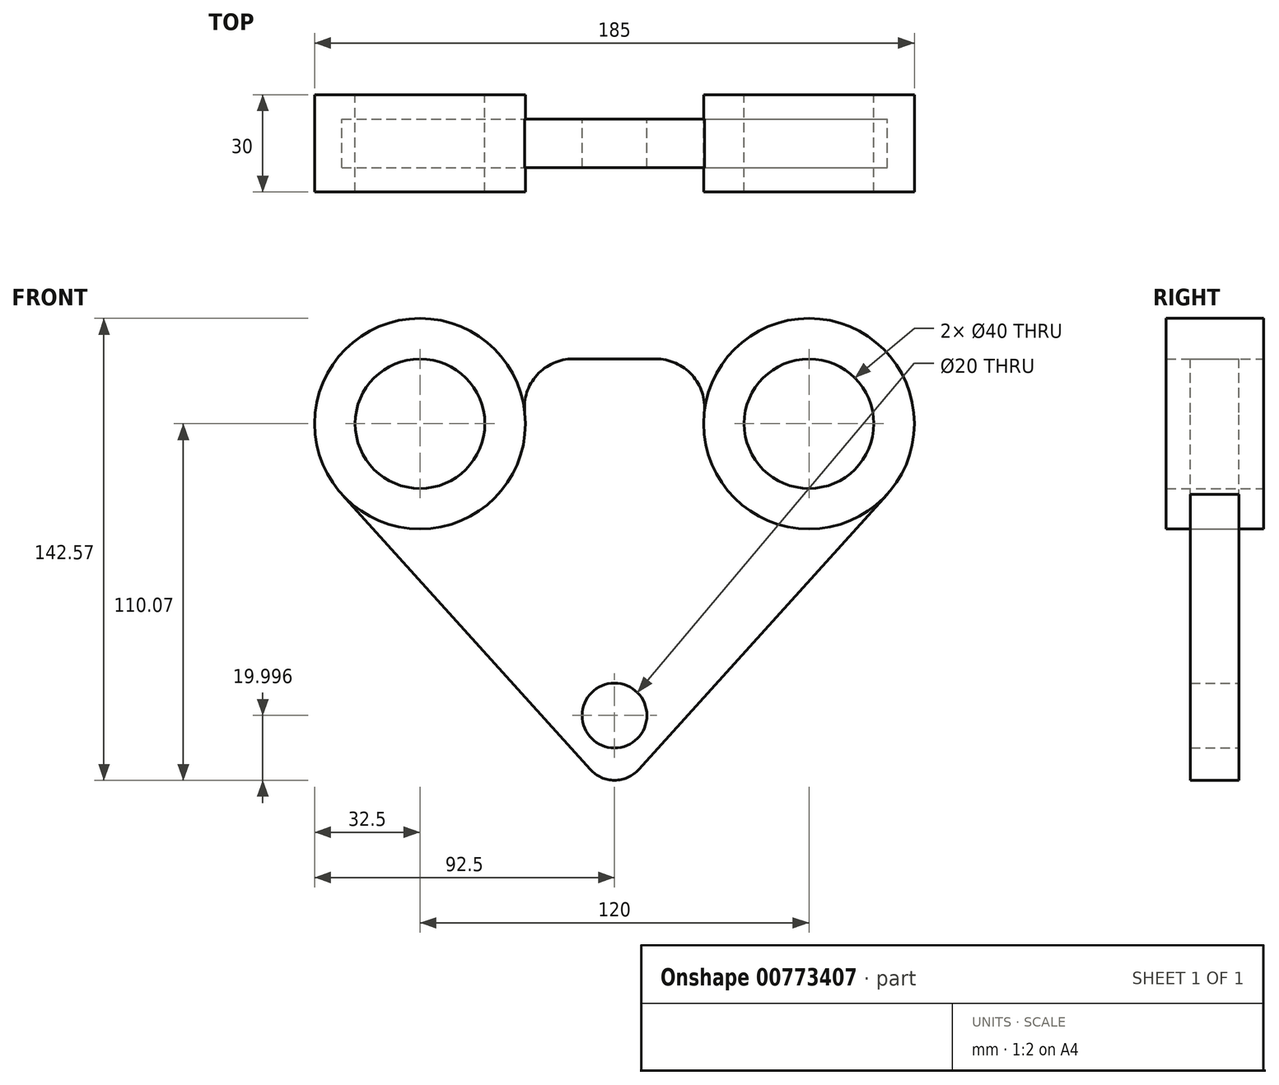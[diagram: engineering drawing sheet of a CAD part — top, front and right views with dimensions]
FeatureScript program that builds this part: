
annotation { "Feature Type Name" : "Feature", "Feature Type Description" : "" }
export const myFeature = defineFeature(function(context is Context, id is Id, definition is map)
    precondition{}
    {
        {
            var Q0;
            Q0=qCreatedBy(makeId("Front.planeOp"),FACE);
            var sketch = newSketch(context, id + "F0", { "sketchPlane" : qUnion([Q0])});
            skCircle(sketch, "E0", {"center": v(0, 0) * mm, "radius": 20 * mm});
            skCircle(sketch, "E1", {"center": v(0, 0) * mm, "radius": 32.5 * mm});
            skCircle(sketch, "E2", {"center": v(120, 0) * mm, "radius": 32.5 * mm});
            skCircle(sketch, "E3", {"center": v(120, 0) * mm, "radius": 20 * mm});
            skCircle(sketch, "E4", {"center": v(60, -90.07) * mm, "radius": 10 * mm});
            skLineSegment(sketch, "E5", {"start": v(-24.13, -21.77) * mm, "end": v(52.58, -106.77) * mm});
            skLineSegment(sketch, "E6", {"start": v(67.42, -106.77) * mm, "end": v(144.13, -21.77) * mm});
            skLineSegment(sketch, "E7", {"start": v(25.62, 20) * mm, "end": v(94.38, 20) * mm});
            skArc(sketch, "E8", {"start": v(52.58, -106.77) * mm, "mid": v(60, -110.07) * mm, "end": v(67.42, -106.77) * mm});
            skPoint(sketch, "E9.orphan", {"position": v(60, -115) * mm});
            skSolve(sketch);
        }
        {
            var Q0;
            Q0=makeQuery(id+"F0.imprint","IMPRINT",FACE,{"disambiguationData":[TD([[makeQuery(id+"F0.imprint","IMPRINT",EDGE,{"derivedFrom":sQuery(id+"F0.wireOp",EDGE,"E0")}),-1.0]])]});
            var Q1;
            Q1=makeQuery(id+"F0.imprint","IMPRINT",FACE,{"disambiguationData":[TD([[makeQuery(id+"F0.imprint","IMPRINT",EDGE,{"derivedFrom":sQuery(id+"F0.wireOp",EDGE,"E3")}),-1.0]])]});
            extrude(context, id + "F1", {"entities" : qUnion([Q0, Q1]), "depth" : 30 * mm, "offsetDistance" : 25 * mm, "symmetric" : true});
        }
        {
            var Q0;
            Q0=makeQuery(id+"F0.imprint","IMPRINT",FACE,{"disambiguationData":[TD([[makeQuery(id+"F0.imprint","IMPRINT",EDGE,{"derivedFrom":sQuery(id+"F0.wireOp",EDGE,"E4")}),-1.0]])]});
            extrude(context, id + "F2", {"entities" : qUnion([Q0]), "depth" : 15 * mm, "offsetDistance" : 25 * mm, "symmetric" : true});
        }
        {
            var Q0;
            Q0=makeQuery(id+"F2.opExtrude","SWEPT_EDGE",EDGE,{"disambiguationData":[OSD([sQuery(id+"F0.wireOp",EDGE,"E1"),sQuery(id+"F0.wireOp",EDGE,"E7")])]});
            var Q1;
            Q1=makeQuery(id+"F2.opExtrude","SWEPT_EDGE",EDGE,{"disambiguationData":[OSD([sQuery(id+"F0.wireOp",EDGE,"E2"),sQuery(id+"F0.wireOp",EDGE,"E7")])]});
            fillet(context, id + "F3", {"entities" : qUnion([Q0, Q1]), "radius" : 15 * mm, "tangentPropagation" : true, "allowEdgeOverflow" : false});
        }
    });
